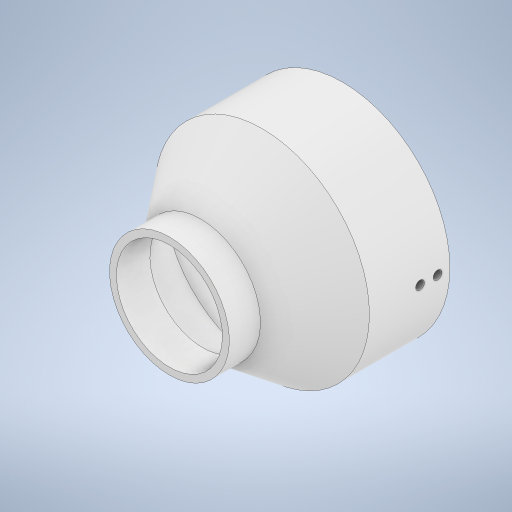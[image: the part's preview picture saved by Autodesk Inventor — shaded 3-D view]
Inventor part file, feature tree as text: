
AUTODESK INVENTOR PART (.ipt)
format: ipt  version: 2023 (Build 270158030, 158C)  size: 276,480 bytes
history: native  units: in
note: dims shown in document units (in); Inventor stores cm internally (conversion verified against a paired STEP export)
features: sketch x2, revolve x1, extrude x1
ambient origin geometry x8: Origin, YZ Plane, XZ Plane, XY Plane, X Axis, Y Axis, Z Axis, Center Point
bodies: Solid1 (feature_tree)
feature tree (4):
  revolve  "Revolution1"  [1 undecoded]
  extrude  "Extrusion1"  Depth=0.3937in
  sketch  "Sketch1"  dims[d0=2.375in d1=4.5in]
  sketch  "Sketch3"  dims[d2=0.75in d3=1.75in d4=0.154in d5=3.88in d6=2.0in d7=90.0deg d8=0.1969in d9=0.1969in d10=0.2756in d11=0.3937in d12=0.0in d13=0.0in]
note: 1 required parameter value undecoded (feature->parameter linkage not recoverable at this tier; creation-order binding heuristic only, values carry confidence <= 0.55)
